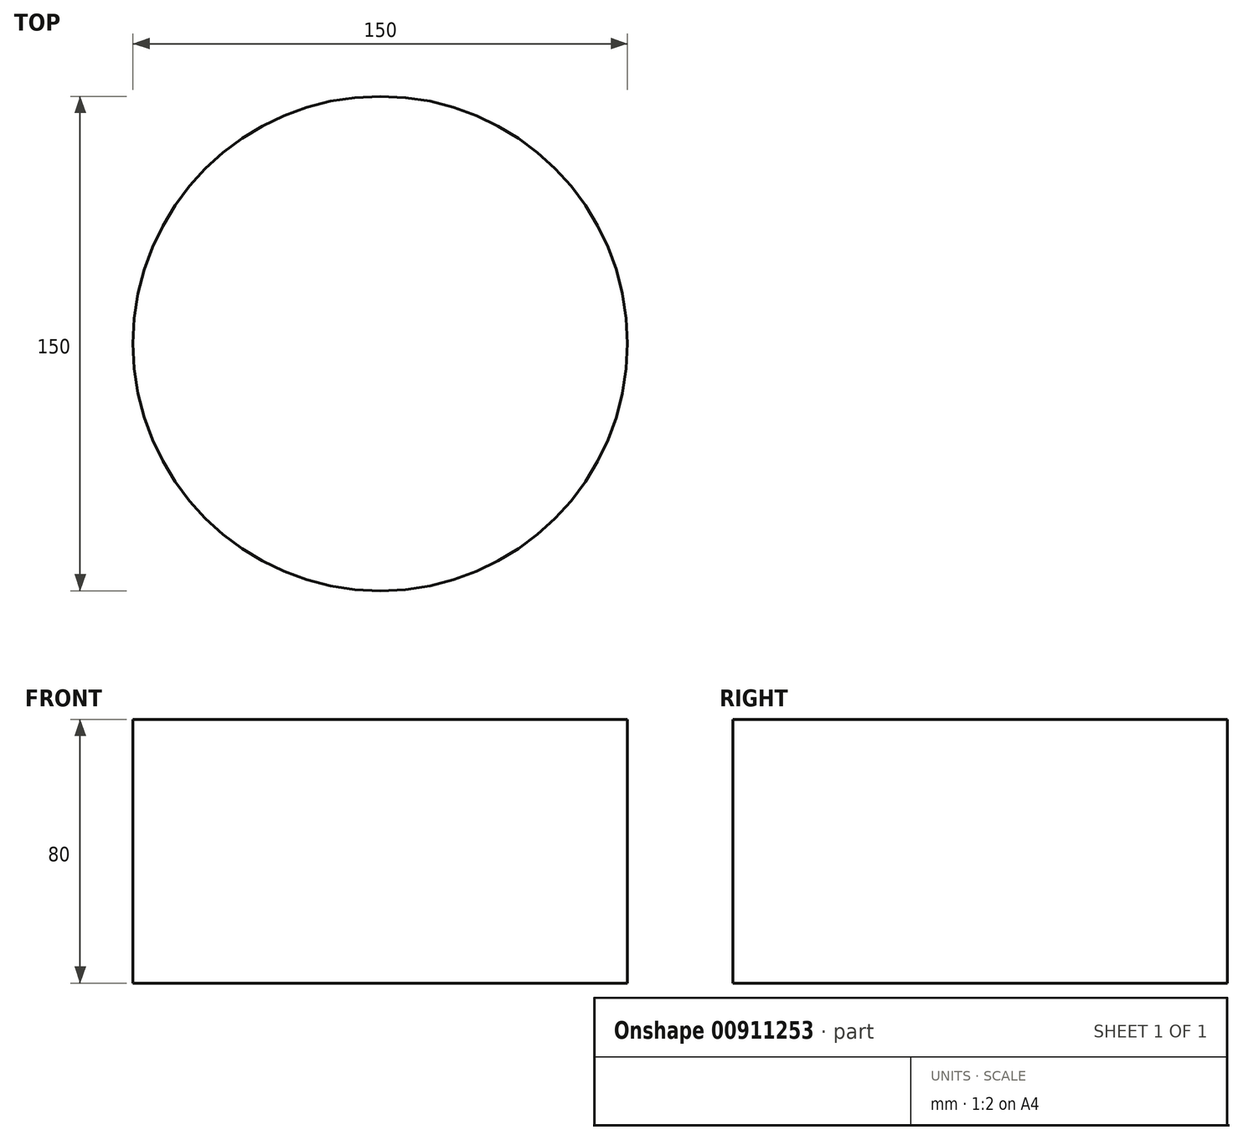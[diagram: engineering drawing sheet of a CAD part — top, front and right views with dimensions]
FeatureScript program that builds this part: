
annotation { "Feature Type Name" : "Feature", "Feature Type Description" : "" }
export const myFeature = defineFeature(function(context is Context, id is Id, definition is map)
    precondition{}
    {
        {
            var Q0;
            Q0=qCreatedBy(makeId("Top.planeOp"),FACE);
            var sketch = newSketch(context, id + "F0", { "sketchPlane" : qUnion([Q0])});
            skCircle(sketch, "E0", {"center": v(0, 0) * mm, "radius": 75 * mm});
            skSolve(sketch);
        }
        {
            var Q0;
            Q0=makeQuery(id+"F0.imprint","IMPRINT",FACE,{"disambiguationData":[TD([[makeQuery(id+"F0.imprint","IMPRINT",EDGE,{"derivedFrom":sQuery(id+"F0.wireOp",EDGE,"E0")}),1.0]])]});
            extrude(context, id + "F1", {"entities" : qUnion([Q0]), "depth" : 80 * mm, "offsetDistance" : 25 * mm});
        }
    });
